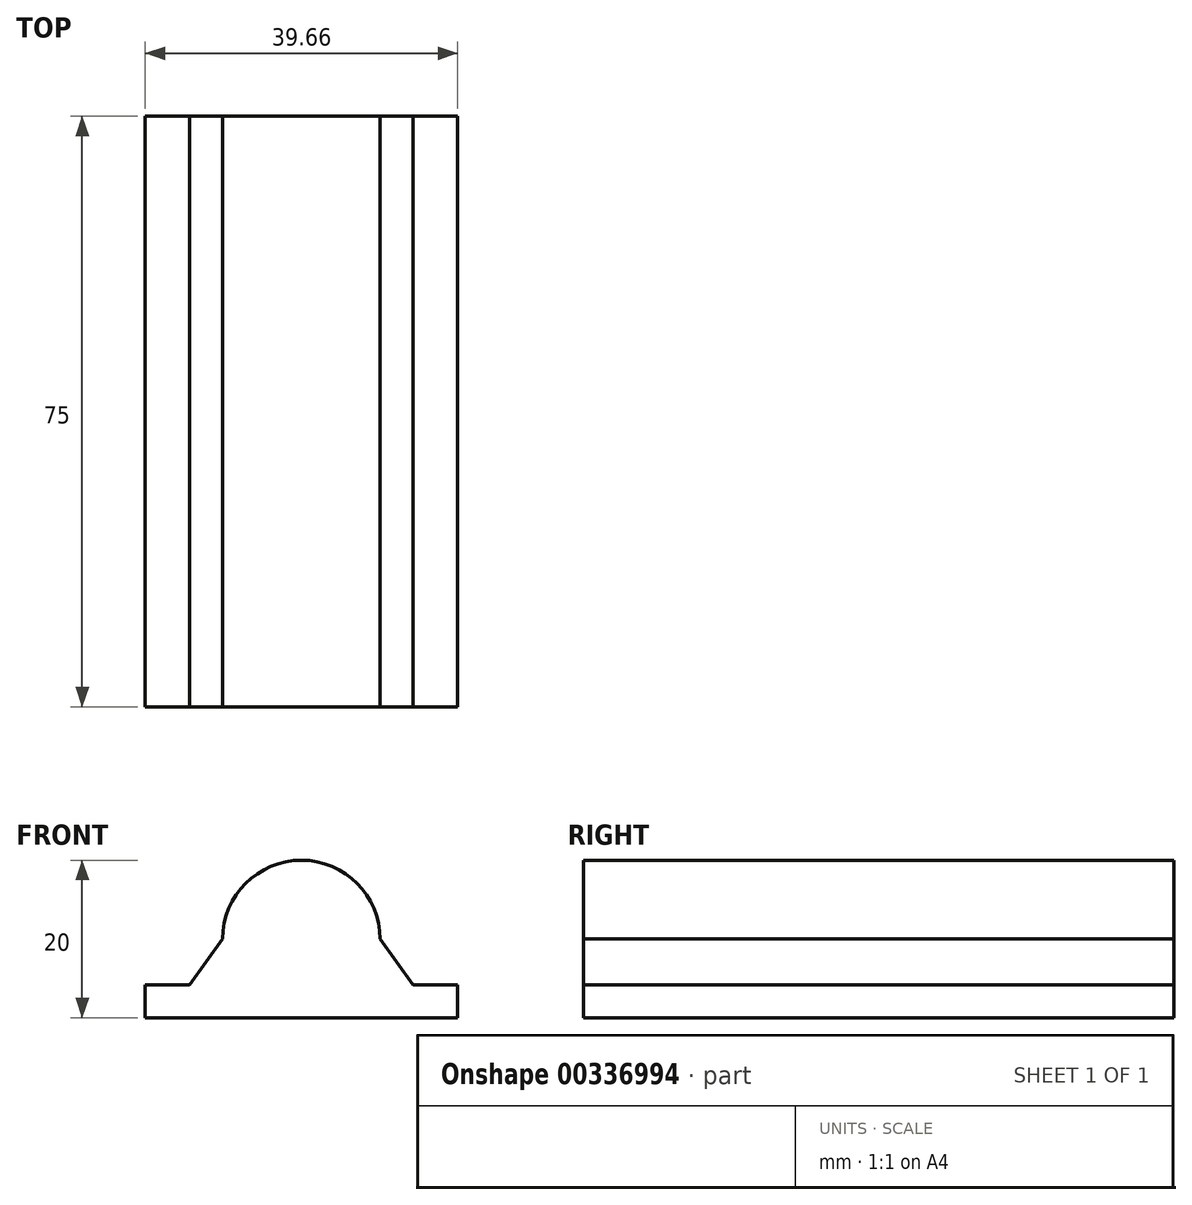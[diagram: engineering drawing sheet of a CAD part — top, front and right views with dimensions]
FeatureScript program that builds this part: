
annotation { "Feature Type Name" : "Feature", "Feature Type Description" : "" }
export const myFeature = defineFeature(function(context is Context, id is Id, definition is map)
    precondition{}
    {
        {
            var Q0;
            Q0=qCreatedBy(makeId("Front.planeOp"),FACE);
            var sketch = newSketch(context, id + "F0", { "sketchPlane" : qUnion([Q0])});
            skCircle(sketch, "E0", {"center": v(0, 0) * mm, "radius": 10 * mm});
            skLineSegment(sketch, "E1.bottom", {"start": v(0, -10) * mm, "end": v(-19.83, -10) * mm});
            skLineSegment(sketch, "E1.top", {"start": v(0, -5.84) * mm, "end": v(-19.83, -5.84) * mm});
            skLineSegment(sketch, "E1.left", {"start": v(0, -10) * mm, "end": v(0, -5.84) * mm});
            skLineSegment(sketch, "E1.right", {"start": v(-19.83, -10) * mm, "end": v(-19.83, -5.84) * mm});
            skLineSegment(sketch, "E2.MirrorCS", {"start": v(0, -5.84) * mm, "end": v(19.83, -5.84) * mm});
            skLineSegment(sketch, "E3.MirrorCS", {"start": v(19.83, -10) * mm, "end": v(19.83, -5.84) * mm});
            skLineSegment(sketch, "E4.MirrorCS", {"start": v(0, -10) * mm, "end": v(19.83, -10) * mm});
            skLineSegment(sketch, "E5", {"start": v(-14.21, -5.84) * mm, "end": v(-10, 0) * mm});
            skLineSegment(sketch, "E6.MirrorCS", {"start": v(14.21, -5.84) * mm, "end": v(10, 0) * mm});
            skSolve(sketch);
        }
        {
            var Q0;
            Q0 = qSketchRegion(id + "F0", true);
            extrude(context, id + "F1", {"entities" : qUnion([Q0]), "depth" : 75 * mm});
        }
    });
